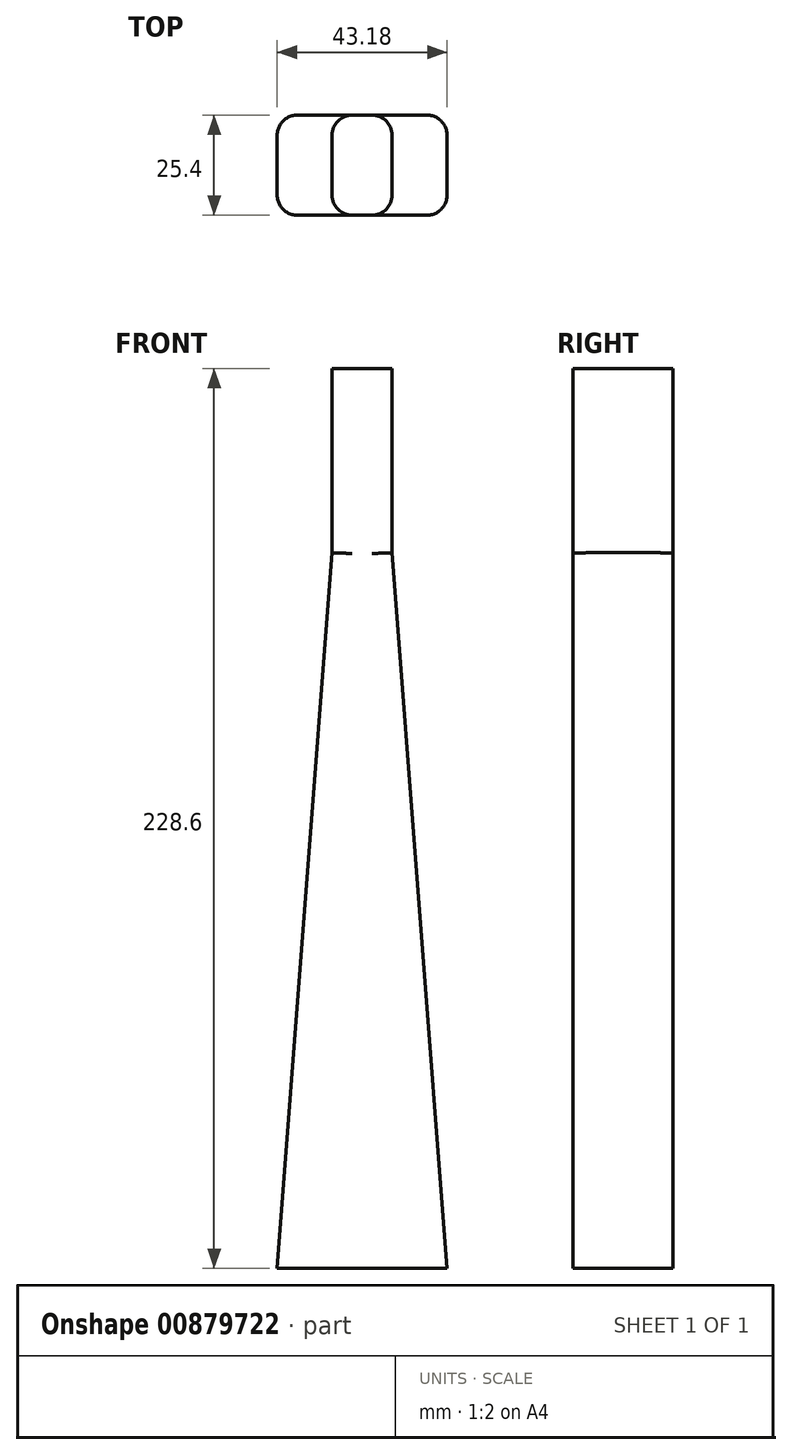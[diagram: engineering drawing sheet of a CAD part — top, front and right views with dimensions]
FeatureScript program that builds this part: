
annotation { "Feature Type Name" : "Feature", "Feature Type Description" : "" }
export const myFeature = defineFeature(function(context is Context, id is Id, definition is map)
    precondition{}
    {
        {
            var Q0;
            Q0=qCreatedBy(makeId("Front.planeOp"),FACE);
            var sketch = newSketch(context, id + "F0", { "sketchPlane" : qUnion([Q0])});
            skLineSegment(sketch, "E0", {"start": v(0, 0) * mm, "end": v(0, 228.6) * mm});
            skLineSegment(sketch, "E1", {"start": v(0, 228.6) * mm, "end": v(7.62, 228.6) * mm});
            skLineSegment(sketch, "E2", {"start": v(7.62, 228.6) * mm, "end": v(7.62, 210.6) * mm});
            skLineSegment(sketch, "E3", {"start": v(7.62, 210.6) * mm, "end": v(7.62, 181.82) * mm});
            skLineSegment(sketch, "E4", {"start": v(7.62, 181.82) * mm, "end": v(21.6, 0) * mm});
            skLineSegment(sketch, "E5", {"start": v(0, 0) * mm, "end": v(21.59, 0) * mm});
            skSolve(sketch);
        }
        {
            var Q0;
            Q0=makeQuery(id+"F0.imprint","IMPRINT",FACE,{"disambiguationData":[TD([[makeQuery(id+"F0.imprint","IMPRINT",EDGE,{"derivedFrom":sQuery(id+"F0.wireOp",EDGE,"E0")}),-1.0]])]});
            extrude(context, id + "F1", {"entities" : qUnion([Q0]), "depth" : 12.7 * mm, "offsetDistance" : 25.4 * mm});
        }
        {
            var Q0;
            Q0=makeQuery(id+"F1.opExtrude","SWEPT_BODY",BODY,{"disambiguationData":[OSD([sQuery(id+"F0.wireOp",EDGE,"E0"),sQuery(id+"F0.wireOp",EDGE,"E1"),sQuery(id+"F0.wireOp",EDGE,"E2"),sQuery(id+"F0.wireOp",EDGE,"E3"),sQuery(id+"F0.wireOp",EDGE,"E4"),sQuery(id+"F0.wireOp",EDGE,"E5")])]});
            var Q1;
            Q1=qCreatedBy(makeId("Front.planeOp"),FACE);
            mirror(context, id + "F2", {"operationType" : NewBodyOperationType.ADD, "entities" : qUnion([Q0]), "mirrorPlane" : qUnion([Q1])});
        }
        {
            var Q0;
            Q0=makeQuery(id+"F1.opExtrude","SWEPT_BODY",BODY,{"disambiguationData":[OSD([sQuery(id+"F0.wireOp",EDGE,"E0"),sQuery(id+"F0.wireOp",EDGE,"E1"),sQuery(id+"F0.wireOp",EDGE,"E2"),sQuery(id+"F0.wireOp",EDGE,"E3"),sQuery(id+"F0.wireOp",EDGE,"E4"),sQuery(id+"F0.wireOp",EDGE,"E5")])]});
            var Q1;
            Q1=qCreatedBy(makeId("Right.planeOp"),FACE);
            mirror(context, id + "F3", {"operationType" : NewBodyOperationType.ADD, "entities" : qUnion([Q0]), "mirrorPlane" : qUnion([Q1])});
        }
        {
            var Q0;
            Q0=makeQuery(id+"F1.opExtrude","CAP_EDGE",EDGE,{"disambiguationData":[OSD([sQuery(id+"F0.wireOp",EDGE,"E4")])],"isStart":false});
            var Q1;
            Q1=makeQuery(id+"F3.opPattern","COPY",EDGE,{"derivedFrom":makeQuery(id+"F1.opExtrude","CAP_EDGE",EDGE,{"disambiguationData":[OSD([sQuery(id+"F0.wireOp",EDGE,"E4")])],"isStart":false}),"instanceName":"1"});
            var Q2;
            Q2=makeQuery(id+"F2.opPattern","COPY",EDGE,{"derivedFrom":makeQuery(id+"F1.opExtrude","CAP_EDGE",EDGE,{"disambiguationData":[OSD([sQuery(id+"F0.wireOp",EDGE,"E4")])],"isStart":false}),"instanceName":"1"});
            var Q3;
            Q3=makeQuery(id+"F3.opPattern","COPY",EDGE,{"derivedFrom":makeQuery(id+"F2.opPattern","COPY",EDGE,{"derivedFrom":makeQuery(id+"F1.opExtrude","CAP_EDGE",EDGE,{"disambiguationData":[OSD([sQuery(id+"F0.wireOp",EDGE,"E4")])],"isStart":false}),"instanceName":"1"}),"instanceName":"1"});
            fillet(context, id + "F4", {"entities" : qUnion([Q0, Q1, Q2, Q3]), "radius" : 5.08 * mm, "tangentPropagation" : true, "allowEdgeOverflow" : false});
        }
        {
            var Q0;
            Q0=makeQuery(id+"F2.opPattern","COPY",EDGE,{"derivedFrom":makeQuery(id+"F1.opExtrude","CAP_EDGE",EDGE,{"disambiguationData":[OSD([sQuery(id+"F0.wireOp",EDGE,"E2"),sQuery(id+"F0.wireOp",EDGE,"E3")])],"isStart":false}),"instanceName":"1"});
            var Q1;
            Q1=makeQuery(id+"F3.opPattern","COPY",EDGE,{"derivedFrom":makeQuery(id+"F2.opPattern","COPY",EDGE,{"derivedFrom":makeQuery(id+"F1.opExtrude","CAP_EDGE",EDGE,{"disambiguationData":[OSD([sQuery(id+"F0.wireOp",EDGE,"E2"),sQuery(id+"F0.wireOp",EDGE,"E3")])],"isStart":false}),"instanceName":"1"}),"instanceName":"1"});
            var Q2;
            Q2=makeQuery(id+"F1.opExtrude","CAP_EDGE",EDGE,{"disambiguationData":[OSD([sQuery(id+"F0.wireOp",EDGE,"E2"),sQuery(id+"F0.wireOp",EDGE,"E3")])],"isStart":false});
            var Q3;
            Q3=makeQuery(id+"F3.opPattern","COPY",EDGE,{"derivedFrom":makeQuery(id+"F1.opExtrude","CAP_EDGE",EDGE,{"disambiguationData":[OSD([sQuery(id+"F0.wireOp",EDGE,"E2"),sQuery(id+"F0.wireOp",EDGE,"E3")])],"isStart":false}),"instanceName":"1"});
            fillet(context, id + "F5", {"entities" : qUnion([Q0, Q1, Q2, Q3]), "radius" : 5.08 * mm, "tangentPropagation" : true, "allowEdgeOverflow" : false});
        }
    });
